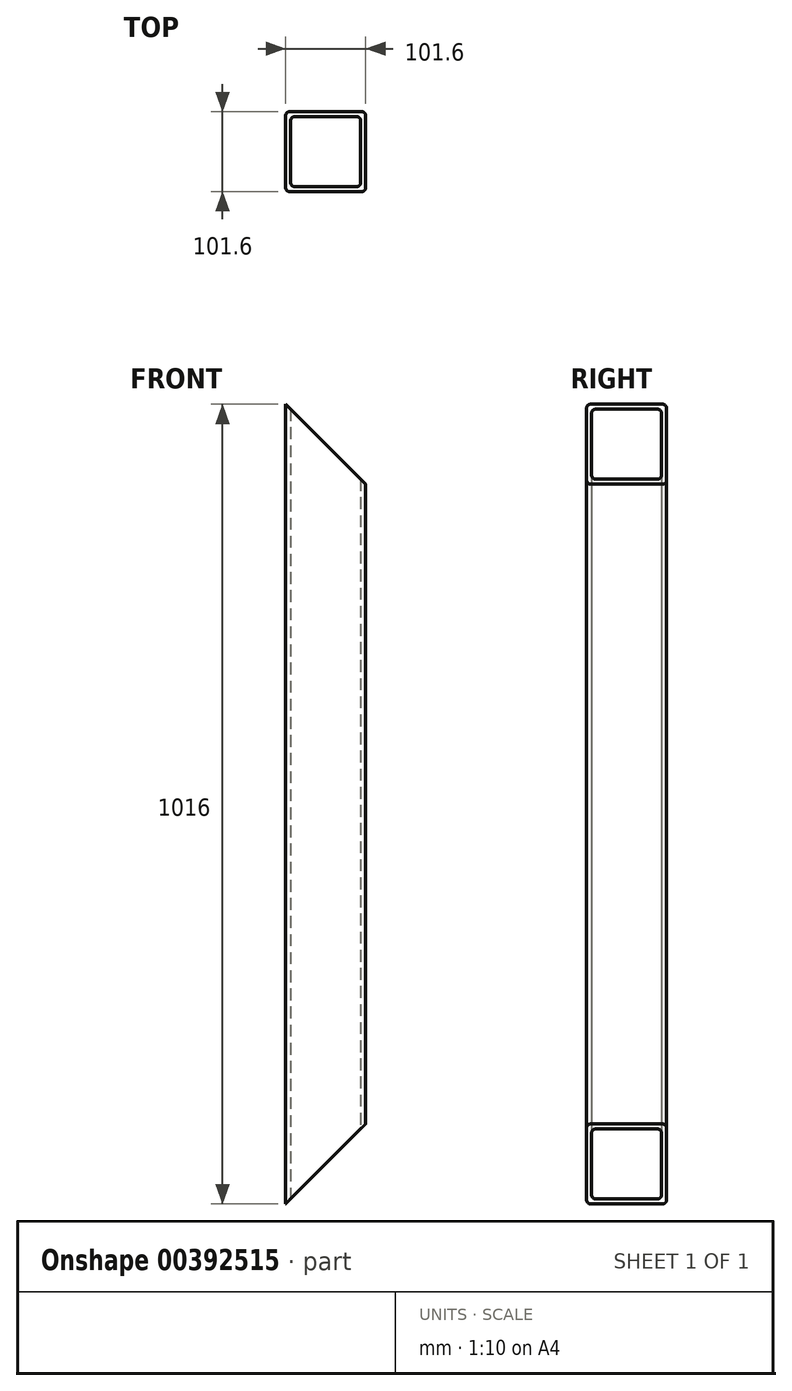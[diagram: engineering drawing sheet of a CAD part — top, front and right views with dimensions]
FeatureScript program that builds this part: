
annotation { "Feature Type Name" : "Feature", "Feature Type Description" : "" }
export const myFeature = defineFeature(function(context is Context, id is Id, definition is map)
    precondition{}
    {
        {
            var Q0;
            Q0=qCreatedBy(makeId("Top.planeOp"),FACE);
            var sketch = newSketch(context, id + "F0", { "sketchPlane" : qUnion([Q0])});
            skLineSegment(sketch, "E0.bottom", {"start": v(50.8, -50.8) * mm, "end": v(-50.8, -50.8) * mm});
            skLineSegment(sketch, "E0.top", {"start": v(50.8, 50.8) * mm, "end": v(-50.8, 50.8) * mm});
            skLineSegment(sketch, "E0.left", {"start": v(50.8, -50.8) * mm, "end": v(50.8, 50.8) * mm});
            skLineSegment(sketch, "E0.right", {"start": v(-50.8, -50.8) * mm, "end": v(-50.8, 50.8) * mm});
            skPoint(sketch, "E0.middle", {"position": v(0, 0) * mm});
            skLineSegment(sketch, "E1.bottom", {"start": v(44.45, -44.45) * mm, "end": v(-44.45, -44.45) * mm});
            skLineSegment(sketch, "E1.top", {"start": v(44.45, 44.45) * mm, "end": v(-44.45, 44.45) * mm});
            skLineSegment(sketch, "E1.left", {"start": v(44.45, -44.45) * mm, "end": v(44.45, 44.45) * mm});
            skLineSegment(sketch, "E1.right", {"start": v(-44.45, -44.45) * mm, "end": v(-44.45, 44.45) * mm});
            skSolve(sketch);
        }
        {
            var Q0;
            Q0 = qSketchRegion(id + "F0", true);
            extrude(context, id + "F1", {"entities" : qUnion([Q0]), "endBound" : BoundingType.SYMMETRIC, "depth" : 1016 * mm});
        }
        {
            var Q0;
            Q0=makeQuery(id+"F1.opExtrude","SWEPT_FACE",FACE,{"disambiguationData":[OSD([sQuery(id+"F0.wireOp",EDGE,"E0.bottom")])]});
            var sketch = newSketch(context, id + "F2", { "sketchPlane" : qUnion([Q0])});
            skPoint(sketch, "E2.0", {"position": v(-50.8, 508) * mm});
            skPoint(sketch, "E3.0", {"position": v(-50.8, -508) * mm});
            skLineSegment(sketch, "E4", {"start": v(-50.8, -508) * mm, "end": v(51.11, -508) * mm});
            skLineSegment(sketch, "E5", {"start": v(-50.8, -508) * mm, "end": v(74.35, -382.85) * mm});
            skLineSegment(sketch, "E6", {"start": v(-50.8, 508) * mm, "end": v(79.52, 377.68) * mm});
            skSolve(sketch);
        }
        {
            var Q0;
            {var subQ1=sQuery(id+"F0.wireOp",EDGE,"E0.bottom");var subQ2=makeQuery(id+"F1.opExtrude","CAP_EDGE",EDGE,{"disambiguationData":[OSD([subQ1])],"isStart":false});Q0=makeQuery(id+"F2.imprint","IMPRINT",FACE,{"disambiguationData":[TD([[makeQuery(id+"F2.imprint","IMPRINT",EDGE,{"derivedFrom":subQ2}),1.0]])]});}
            var Q1;
            {var subQ0=sQuery(id+"F2.wireOp",EDGE,"E4");var subQ1=sQuery(id+"F0.wireOp",EDGE,"E0.bottom");var subQ2=makeQuery(id+"F1.opExtrude","SWEPT_EDGE",EDGE,{"disambiguationData":[OSD([subQ1,sQuery(id+"F0.wireOp",EDGE,"E0.left")])]});var subQ3=makeQuery(id+"F2.imprint","INTERSECT",VERTEX,{"derivedFrom":[subQ2,subQ0]});Q1=makeQuery(id+"F2.imprint","IMPRINT",FACE,{"disambiguationData":[TD([[makeQuery(id+"F2.imprint","IMPRINT",EDGE,{"disambiguationData":[TD([[subQ3,-1.0]])],"derivedFrom":subQ0}),-1.0]])]});}
            extrude(context, id + "F3", {"entities" : qUnion([Q0, Q1]), "operationType" : NewBodyOperationType.REMOVE, "endBound" : BoundingType.THROUGH_ALL, "oppositeDirection" : true, "depth" : 25.4 * mm});
        }
        {
            var Q0;
            Q0=makeQuery(id+"F1.opExtrude","SWEPT_EDGE",EDGE,{"disambiguationData":[OSD([sQuery(id+"F0.wireOp",EDGE,"E0.bottom"),sQuery(id+"F0.wireOp",EDGE,"E0.right")])]});
            var Q1;
            Q1=makeQuery(id+"F1.opExtrude","SWEPT_EDGE",EDGE,{"disambiguationData":[OSD([sQuery(id+"F0.wireOp",EDGE,"E0.bottom"),sQuery(id+"F0.wireOp",EDGE,"E0.left")])]});
            var Q2;
            Q2=makeQuery(id+"F1.opExtrude","SWEPT_EDGE",EDGE,{"disambiguationData":[OSD([sQuery(id+"F0.wireOp",EDGE,"E0.top"),sQuery(id+"F0.wireOp",EDGE,"E0.right")])]});
            var Q3;
            Q3=makeQuery(id+"F1.opExtrude","SWEPT_EDGE",EDGE,{"disambiguationData":[OSD([sQuery(id+"F0.wireOp",EDGE,"E0.top"),sQuery(id+"F0.wireOp",EDGE,"E0.left")])]});
            var Q4;
            Q4=makeQuery(id+"F1.opExtrude","SWEPT_EDGE",EDGE,{"disambiguationData":[OSD([sQuery(id+"F0.wireOp",EDGE,"E1.top"),sQuery(id+"F0.wireOp",EDGE,"E1.left")])]});
            var Q5;
            Q5=makeQuery(id+"F1.opExtrude","SWEPT_EDGE",EDGE,{"disambiguationData":[OSD([sQuery(id+"F0.wireOp",EDGE,"E1.top"),sQuery(id+"F0.wireOp",EDGE,"E1.right")])]});
            var Q6;
            Q6=makeQuery(id+"F1.opExtrude","SWEPT_EDGE",EDGE,{"disambiguationData":[OSD([sQuery(id+"F0.wireOp",EDGE,"E1.bottom"),sQuery(id+"F0.wireOp",EDGE,"E1.right")])]});
            var Q7;
            Q7=makeQuery(id+"F1.opExtrude","SWEPT_EDGE",EDGE,{"disambiguationData":[OSD([sQuery(id+"F0.wireOp",EDGE,"E1.bottom"),sQuery(id+"F0.wireOp",EDGE,"E1.left")])]});
            fillet(context, id + "F4", {"entities" : qUnion([Q0, Q1, Q2, Q3, Q4, Q5, Q6, Q7]), "radius" : 5.08 * mm, "tangentPropagation" : true, "allowEdgeOverflow" : false});
        }
    });
